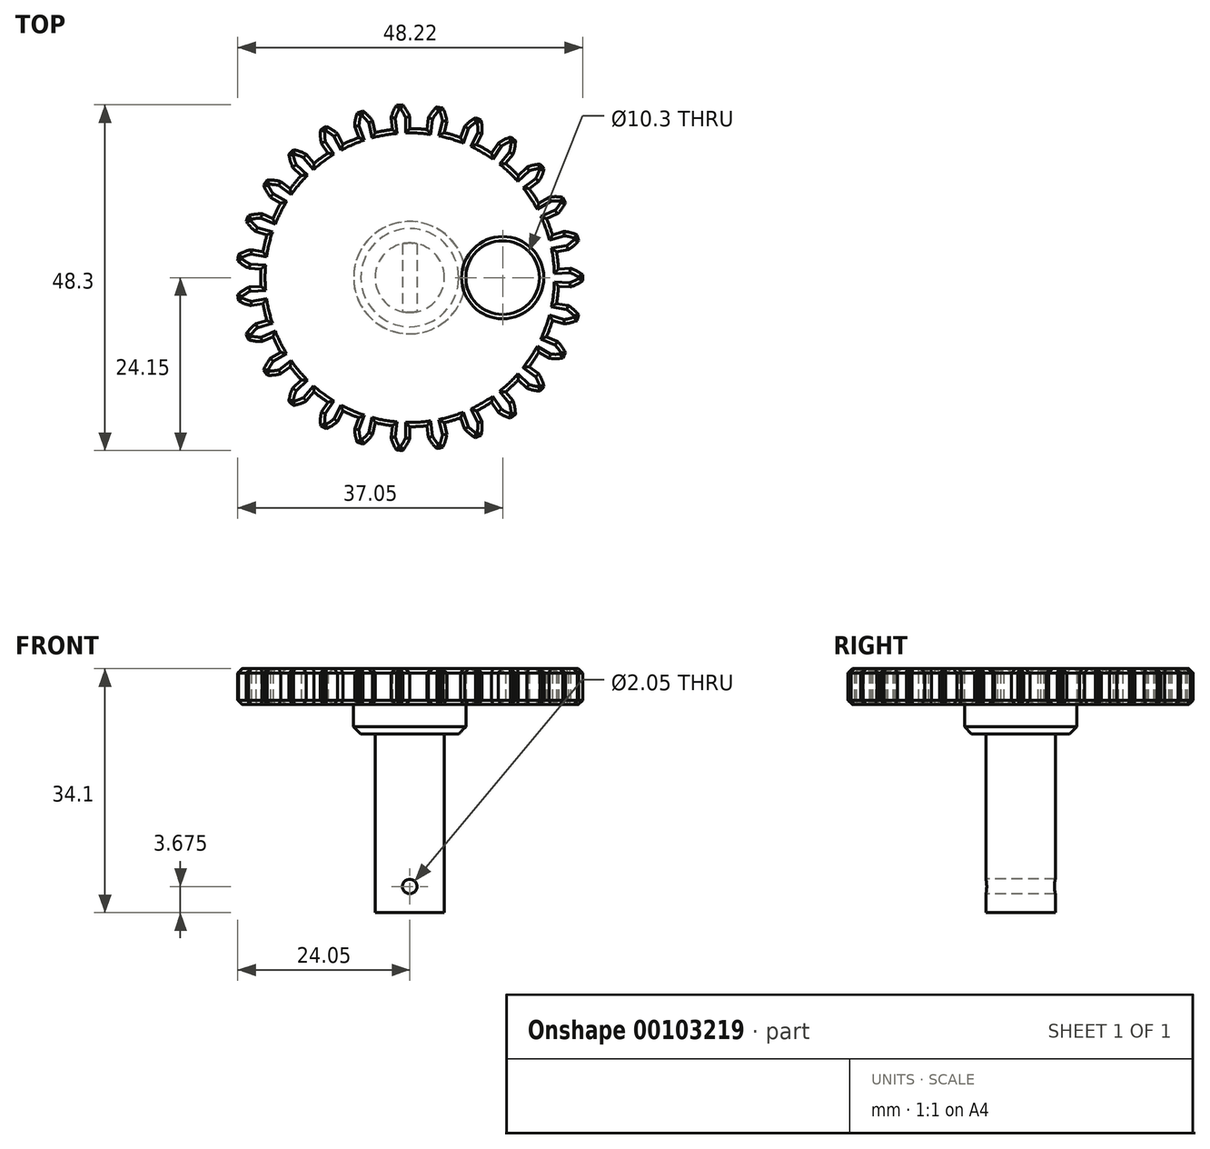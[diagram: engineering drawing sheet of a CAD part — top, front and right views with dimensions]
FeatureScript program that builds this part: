
annotation { "Feature Type Name" : "Feature", "Feature Type Description" : "" }
export const myFeature = defineFeature(function(context is Context, id is Id, definition is map)
    precondition{}
    {
        {
            assignVariable(context, id + "F0", {"name" : "PrintingOffset", "anyValue" : 0.3});
        }
        {
            assignVariable(context, id + "F1", {"name" : "ClampThickness", "anyValue" : 20});
        }
        {
            assignVariable(context, id + "F2", {"name" : "FilamentDiameter", "anyValue" : 1.75 + getVariable(context, 'PrintingOffset')});
        }
        {
            assignVariable(context, id + "F3", {"name" : "CollarThickness", "anyValue" : 2 * getVariable(context, 'FilamentDiameter')});
        }
        {
            assignVariable(context, id + "F4", {"name" : "GearThickness", "anyValue" : 5});
        }
        {
            var Q0;
            Q0=qCreatedBy(makeId("Top.planeOp"),FACE);
            var sketch = newSketch(context, id + "F5", { "sketchPlane" : qUnion([Q0])});
            skCircle(sketch, "E0", {"center": v(0, 0) * mm, "radius": 22.5 * mm, "construction": true});
            skCircle(sketch, "E1", {"center": v(0, 0) * mm, "radius": 20.83 * mm});
            skCircle(sketch, "E2", {"center": v(0, 0) * mm, "radius": 24.17 * mm, "construction": true});
            skLineSegment(sketch, "E3", {"start": v(0, 0) * mm, "end": v(0, 28.6) * mm, "construction": true});
            skLineSegment(sketch, "E4", {"start": v(0, 0) * mm, "end": v(-3.34, 28.6) * mm, "construction": true});
            skLineSegment(sketch, "E5", {"start": v(-15.46, 22.5) * mm, "end": v(0, 22.5) * mm, "construction": true});
            skLineSegment(sketch, "E6", {"start": v(0, 22.5) * mm, "end": v(-15.46, 16.87) * mm, "construction": true});
            skLineSegment(sketch, "E7", {"start": v(0, 0) * mm, "end": v(-1.67, 28.6) * mm, "construction": true});
            skCircle(sketch, "E8", {"center": v(0, 22.5) * mm, "radius": 5.62 * mm, "construction": true});
            skCircle(sketch, "E9", {"center": v(0, 0) * mm, "radius": 21.14 * mm, "construction": true});
            skArc(sketch, "E10", {"start": v(0, 22.5) * mm, "mid": v(-0.42, 23.37) * mm, "end": v(-0.98, 24.15) * mm});
            skArc(sketch, "E11.trimOffspring", {"start": v(0.36, 20.83) * mm, "mid": v(0.35, 20.99) * mm, "end": v(0.34, 21.14) * mm});
            skArc(sketch, "E12.trimOffspring", {"start": v(-0.98, 16.82) * mm, "mid": v(-0.93, 16.88) * mm, "end": v(-0.88, 16.94) * mm});
            skLineSegment(sketch, "E13", {"start": v(0, 22.5) * mm, "end": v(0, 20.83) * mm});
            skLineSegment(sketch, "E14", {"start": v(-0.98, 24.15) * mm, "end": v(-1.4, 24.13) * mm});
            skLineSegment(sketch, "E15.MirrorCS", {"start": v(-1.83, 24.1) * mm, "end": v(-1.4, 24.13) * mm});
            skArc(sketch, "E16.MirrorCS", {"start": v(-2.61, 22.35) * mm, "mid": v(-2.3, 23.26) * mm, "end": v(-1.83, 24.1) * mm});
            skLineSegment(sketch, "E17.MirrorCS", {"start": v(-2.61, 22.35) * mm, "end": v(-2.42, 20.7) * mm});
            skLineSegment(sketch, "E18.1.0", {"start": v(-5.19, 21.9) * mm, "end": v(-4.8, 20.27) * mm});
            skArc(sketch, "E18.1.1", {"start": v(-5.19, 21.9) * mm, "mid": v(-5.8, 22.64) * mm, "end": v(-6.53, 23.27) * mm});
            skLineSegment(sketch, "E18.1.2", {"start": v(-6.53, 23.27) * mm, "end": v(-6.93, 23.15) * mm});
            skLineSegment(sketch, "E18.1.3", {"start": v(-7.33, 23.03) * mm, "end": v(-6.93, 23.15) * mm});
            skArc(sketch, "E18.1.4", {"start": v(-7.7, 21.14) * mm, "mid": v(-7.6, 22.1) * mm, "end": v(-7.33, 23.03) * mm});
            skLineSegment(sketch, "E18.1.5", {"start": v(-7.7, 21.14) * mm, "end": v(-7.13, 19.58) * mm});
            skLineSegment(sketch, "E18.2.0", {"start": v(-10.1, 20.1) * mm, "end": v(-9.35, 18.62) * mm});
            skArc(sketch, "E18.2.1", {"start": v(-10.1, 20.1) * mm, "mid": v(-10.86, 20.7) * mm, "end": v(-11.72, 21.14) * mm});
            skLineSegment(sketch, "E18.2.2", {"start": v(-11.72, 21.14) * mm, "end": v(-12.09, 20.93) * mm});
            skLineSegment(sketch, "E18.2.3", {"start": v(-12.45, 20.71) * mm, "end": v(-12.09, 20.93) * mm});
            skArc(sketch, "E18.2.4", {"start": v(-12.36, 18.8) * mm, "mid": v(-12.49, 19.75) * mm, "end": v(-12.45, 20.71) * mm});
            skLineSegment(sketch, "E18.2.5", {"start": v(-12.36, 18.8) * mm, "end": v(-11.45, 17.4) * mm});
            skLineSegment(sketch, "E18.3.0", {"start": v(-14.46, 17.24) * mm, "end": v(-13.4, 15.96) * mm});
            skArc(sketch, "E18.3.1", {"start": v(-14.46, 17.24) * mm, "mid": v(-15.34, 17.63) * mm, "end": v(-16.27, 17.87) * mm});
            skLineSegment(sketch, "E18.3.2", {"start": v(-16.27, 17.87) * mm, "end": v(-16.59, 17.58) * mm});
            skLineSegment(sketch, "E18.3.3", {"start": v(-16.89, 17.29) * mm, "end": v(-16.59, 17.58) * mm});
            skArc(sketch, "E18.3.4", {"start": v(-16.37, 15.44) * mm, "mid": v(-16.7, 16.34) * mm, "end": v(-16.89, 17.29) * mm});
            skLineSegment(sketch, "E18.3.5", {"start": v(-16.37, 15.44) * mm, "end": v(-15.15, 14.3) * mm});
            skLineSegment(sketch, "E18.4.0", {"start": v(-18.05, 13.44) * mm, "end": v(-16.71, 12.44) * mm});
            skArc(sketch, "E18.4.1", {"start": v(-18.05, 13.44) * mm, "mid": v(-19, 13.62) * mm, "end": v(-19.96, 13.63) * mm});
            skLineSegment(sketch, "E18.4.2", {"start": v(-19.96, 13.63) * mm, "end": v(-20.2, 13.28) * mm});
            skLineSegment(sketch, "E18.4.3", {"start": v(-20.42, 12.93) * mm, "end": v(-20.2, 13.28) * mm});
            skArc(sketch, "E18.4.4", {"start": v(-19.49, 11.25) * mm, "mid": v(-20.02, 12.05) * mm, "end": v(-20.42, 12.93) * mm});
            skLineSegment(sketch, "E18.4.5", {"start": v(-19.49, 11.25) * mm, "end": v(-18.04, 10.42) * mm});
            skLineSegment(sketch, "E18.5.0", {"start": v(-20.66, 8.91) * mm, "end": v(-19.13, 8.25) * mm});
            skArc(sketch, "E18.5.1", {"start": v(-20.66, 8.91) * mm, "mid": v(-21.62, 8.87) * mm, "end": v(-22.56, 8.66) * mm});
            skLineSegment(sketch, "E18.5.2", {"start": v(-22.56, 8.66) * mm, "end": v(-22.71, 8.27) * mm});
            skLineSegment(sketch, "E18.5.3", {"start": v(-22.85, 7.87) * mm, "end": v(-22.71, 8.27) * mm});
            skArc(sketch, "E18.5.4", {"start": v(-21.55, 6.45) * mm, "mid": v(-22.26, 7.1) * mm, "end": v(-22.85, 7.87) * mm});
            skLineSegment(sketch, "E18.5.5", {"start": v(-21.55, 6.45) * mm, "end": v(-19.96, 5.98) * mm});
            skLineSegment(sketch, "E18.6.0", {"start": v(-22.16, 3.9) * mm, "end": v(-20.52, 3.62) * mm});
            skArc(sketch, "E18.6.1", {"start": v(-22.16, 3.9) * mm, "mid": v(-23.08, 3.64) * mm, "end": v(-23.95, 3.22) * mm});
            skLineSegment(sketch, "E18.6.2", {"start": v(-23.95, 3.22) * mm, "end": v(-24, 2.8) * mm});
            skLineSegment(sketch, "E18.6.3", {"start": v(-24.05, 2.39) * mm, "end": v(-24, 2.8) * mm});
            skArc(sketch, "E18.6.4", {"start": v(-22.46, 1.3) * mm, "mid": v(-23.3, 1.78) * mm, "end": v(-24.05, 2.39) * mm});
            skLineSegment(sketch, "E18.6.5", {"start": v(-22.46, 1.3) * mm, "end": v(-20.8, 1.21) * mm});
            skLineSegment(sketch, "E18.7.0", {"start": v(-22.46, -1.3) * mm, "end": v(-20.8, -1.21) * mm});
            skArc(sketch, "E18.7.1", {"start": v(-22.46, -1.3) * mm, "mid": v(-23.3, -1.78) * mm, "end": v(-24.05, -2.39) * mm});
            skLineSegment(sketch, "E18.7.2", {"start": v(-24.05, -2.39) * mm, "end": v(-24, -2.8) * mm});
            skLineSegment(sketch, "E18.7.3", {"start": v(-23.95, -3.22) * mm, "end": v(-24, -2.8) * mm});
            skArc(sketch, "E18.7.4", {"start": v(-22.16, -3.9) * mm, "mid": v(-23.08, -3.64) * mm, "end": v(-23.95, -3.22) * mm});
            skLineSegment(sketch, "E18.7.5", {"start": v(-22.16, -3.9) * mm, "end": v(-20.52, -3.62) * mm});
            skLineSegment(sketch, "E18.8.0", {"start": v(-21.55, -6.45) * mm, "end": v(-19.96, -5.98) * mm});
            skArc(sketch, "E18.8.1", {"start": v(-21.55, -6.45) * mm, "mid": v(-22.26, -7.1) * mm, "end": v(-22.85, -7.87) * mm});
            skLineSegment(sketch, "E18.8.2", {"start": v(-22.85, -7.87) * mm, "end": v(-22.71, -8.27) * mm});
            skLineSegment(sketch, "E18.8.3", {"start": v(-22.56, -8.66) * mm, "end": v(-22.71, -8.27) * mm});
            skArc(sketch, "E18.8.4", {"start": v(-20.66, -8.91) * mm, "mid": v(-21.62, -8.87) * mm, "end": v(-22.56, -8.66) * mm});
            skLineSegment(sketch, "E18.8.5", {"start": v(-20.66, -8.91) * mm, "end": v(-19.13, -8.25) * mm});
            skLineSegment(sketch, "E18.9.0", {"start": v(-19.49, -11.25) * mm, "end": v(-18.04, -10.42) * mm});
            skArc(sketch, "E18.9.1", {"start": v(-19.49, -11.25) * mm, "mid": v(-20.02, -12.05) * mm, "end": v(-20.42, -12.93) * mm});
            skLineSegment(sketch, "E18.9.2", {"start": v(-20.42, -12.93) * mm, "end": v(-20.2, -13.28) * mm});
            skLineSegment(sketch, "E18.9.3", {"start": v(-19.96, -13.63) * mm, "end": v(-20.2, -13.28) * mm});
            skArc(sketch, "E18.9.4", {"start": v(-18.05, -13.44) * mm, "mid": v(-19, -13.62) * mm, "end": v(-19.96, -13.63) * mm});
            skLineSegment(sketch, "E18.9.5", {"start": v(-18.05, -13.44) * mm, "end": v(-16.71, -12.44) * mm});
            skLineSegment(sketch, "E18.10.0", {"start": v(-16.37, -15.44) * mm, "end": v(-15.15, -14.3) * mm});
            skArc(sketch, "E18.10.1", {"start": v(-16.37, -15.44) * mm, "mid": v(-16.7, -16.34) * mm, "end": v(-16.89, -17.29) * mm});
            skLineSegment(sketch, "E18.10.2", {"start": v(-16.89, -17.29) * mm, "end": v(-16.59, -17.58) * mm});
            skLineSegment(sketch, "E18.10.3", {"start": v(-16.27, -17.87) * mm, "end": v(-16.59, -17.58) * mm});
            skArc(sketch, "E18.10.4", {"start": v(-14.46, -17.24) * mm, "mid": v(-15.34, -17.63) * mm, "end": v(-16.27, -17.87) * mm});
            skLineSegment(sketch, "E18.10.5", {"start": v(-14.46, -17.24) * mm, "end": v(-13.4, -15.96) * mm});
            skLineSegment(sketch, "E18.11.0", {"start": v(-12.36, -18.8) * mm, "end": v(-11.45, -17.4) * mm});
            skArc(sketch, "E18.11.1", {"start": v(-12.36, -18.8) * mm, "mid": v(-12.49, -19.75) * mm, "end": v(-12.45, -20.71) * mm});
            skLineSegment(sketch, "E18.11.2", {"start": v(-12.45, -20.71) * mm, "end": v(-12.09, -20.93) * mm});
            skLineSegment(sketch, "E18.11.3", {"start": v(-11.72, -21.14) * mm, "end": v(-12.09, -20.93) * mm});
            skArc(sketch, "E18.11.4", {"start": v(-10.1, -20.1) * mm, "mid": v(-10.86, -20.7) * mm, "end": v(-11.72, -21.14) * mm});
            skLineSegment(sketch, "E18.11.5", {"start": v(-10.1, -20.1) * mm, "end": v(-9.35, -18.62) * mm});
            skLineSegment(sketch, "E18.12.0", {"start": v(-7.7, -21.14) * mm, "end": v(-7.13, -19.58) * mm});
            skArc(sketch, "E18.12.1", {"start": v(-7.7, -21.14) * mm, "mid": v(-7.6, -22.1) * mm, "end": v(-7.33, -23.03) * mm});
            skLineSegment(sketch, "E18.12.2", {"start": v(-7.33, -23.03) * mm, "end": v(-6.93, -23.15) * mm});
            skLineSegment(sketch, "E18.12.3", {"start": v(-6.53, -23.27) * mm, "end": v(-6.93, -23.15) * mm});
            skArc(sketch, "E18.12.4", {"start": v(-5.19, -21.9) * mm, "mid": v(-5.8, -22.64) * mm, "end": v(-6.53, -23.27) * mm});
            skLineSegment(sketch, "E18.12.5", {"start": v(-5.19, -21.9) * mm, "end": v(-4.8, -20.27) * mm});
            skLineSegment(sketch, "E18.13.0", {"start": v(-2.61, -22.35) * mm, "end": v(-2.42, -20.7) * mm});
            skArc(sketch, "E18.13.1", {"start": v(-2.61, -22.35) * mm, "mid": v(-2.3, -23.26) * mm, "end": v(-1.83, -24.1) * mm});
            skLineSegment(sketch, "E18.13.2", {"start": v(-1.83, -24.1) * mm, "end": v(-1.4, -24.13) * mm});
            skLineSegment(sketch, "E18.13.3", {"start": v(-0.98, -24.15) * mm, "end": v(-1.4, -24.13) * mm});
            skArc(sketch, "E18.13.4", {"start": v(0, -22.5) * mm, "mid": v(-0.42, -23.37) * mm, "end": v(-0.98, -24.15) * mm});
            skLineSegment(sketch, "E18.13.5", {"start": v(0, -22.5) * mm, "end": v(0, -20.83) * mm});
            skLineSegment(sketch, "E18.14.0", {"start": v(2.61, -22.35) * mm, "end": v(2.42, -20.7) * mm});
            skArc(sketch, "E18.14.1", {"start": v(2.61, -22.35) * mm, "mid": v(3.13, -23.16) * mm, "end": v(3.78, -23.87) * mm});
            skLineSegment(sketch, "E18.14.2", {"start": v(3.78, -23.87) * mm, "end": v(4.2, -23.8) * mm});
            skLineSegment(sketch, "E18.14.3", {"start": v(4.61, -23.72) * mm, "end": v(4.2, -23.8) * mm});
            skArc(sketch, "E18.14.4", {"start": v(5.19, -21.9) * mm, "mid": v(4.98, -22.83) * mm, "end": v(4.61, -23.72) * mm});
            skLineSegment(sketch, "E18.14.5", {"start": v(5.19, -21.9) * mm, "end": v(4.8, -20.27) * mm});
            skLineSegment(sketch, "E18.15.0", {"start": v(7.7, -21.14) * mm, "end": v(7.13, -19.58) * mm});
            skArc(sketch, "E18.15.1", {"start": v(7.7, -21.14) * mm, "mid": v(8.39, -21.81) * mm, "end": v(9.18, -22.35) * mm});
            skLineSegment(sketch, "E18.15.2", {"start": v(9.18, -22.35) * mm, "end": v(9.57, -22.2) * mm});
            skLineSegment(sketch, "E18.15.3", {"start": v(9.96, -22.02) * mm, "end": v(9.57, -22.2) * mm});
            skArc(sketch, "E18.15.4", {"start": v(10.1, -20.1) * mm, "mid": v(10.11, -21.07) * mm, "end": v(9.96, -22.02) * mm});
            skLineSegment(sketch, "E18.15.5", {"start": v(10.1, -20.1) * mm, "end": v(9.35, -18.62) * mm});
            skLineSegment(sketch, "E18.16.0", {"start": v(12.36, -18.8) * mm, "end": v(11.45, -17.4) * mm});
            skArc(sketch, "E18.16.1", {"start": v(12.36, -18.8) * mm, "mid": v(13.2, -19.3) * mm, "end": v(14.1, -19.63) * mm});
            skLineSegment(sketch, "E18.16.2", {"start": v(14.1, -19.63) * mm, "end": v(14.43, -19.39) * mm});
            skLineSegment(sketch, "E18.16.3", {"start": v(14.77, -19.13) * mm, "end": v(14.43, -19.39) * mm});
            skArc(sketch, "E18.16.4", {"start": v(14.46, -17.24) * mm, "mid": v(14.7, -18.17) * mm, "end": v(14.77, -19.13) * mm});
            skLineSegment(sketch, "E18.16.5", {"start": v(14.46, -17.24) * mm, "end": v(13.4, -15.96) * mm});
            skLineSegment(sketch, "E18.17.0", {"start": v(16.37, -15.44) * mm, "end": v(15.15, -14.3) * mm});
            skArc(sketch, "E18.17.1", {"start": v(16.37, -15.44) * mm, "mid": v(17.28, -15.73) * mm, "end": v(18.24, -15.85) * mm});
            skLineSegment(sketch, "E18.17.2", {"start": v(18.24, -15.85) * mm, "end": v(18.52, -15.54) * mm});
            skLineSegment(sketch, "E18.17.3", {"start": v(18.78, -15.2) * mm, "end": v(18.52, -15.54) * mm});
            skArc(sketch, "E18.17.4", {"start": v(18.05, -13.44) * mm, "mid": v(18.5, -14.3) * mm, "end": v(18.78, -15.2) * mm});
            skLineSegment(sketch, "E18.17.5", {"start": v(18.05, -13.44) * mm, "end": v(16.71, -12.44) * mm});
            skLineSegment(sketch, "E18.18.0", {"start": v(19.49, -11.25) * mm, "end": v(18.04, -10.42) * mm});
            skArc(sketch, "E18.18.1", {"start": v(19.49, -11.25) * mm, "mid": v(20.45, -11.32) * mm, "end": v(21.4, -11.22) * mm});
            skLineSegment(sketch, "E18.18.2", {"start": v(21.4, -11.22) * mm, "end": v(21.6, -10.85) * mm});
            skLineSegment(sketch, "E18.18.3", {"start": v(21.78, -10.47) * mm, "end": v(21.6, -10.85) * mm});
            skArc(sketch, "E18.18.4", {"start": v(20.66, -8.91) * mm, "mid": v(21.29, -9.64) * mm, "end": v(21.78, -10.47) * mm});
            skLineSegment(sketch, "E18.18.5", {"start": v(20.66, -8.91) * mm, "end": v(19.13, -8.25) * mm});
            skLineSegment(sketch, "E18.19.0", {"start": v(21.55, -6.45) * mm, "end": v(19.96, -5.98) * mm});
            skArc(sketch, "E18.19.1", {"start": v(21.55, -6.45) * mm, "mid": v(22.5, -6.3) * mm, "end": v(23.41, -5.98) * mm});
            skLineSegment(sketch, "E18.19.2", {"start": v(23.41, -5.98) * mm, "end": v(23.52, -5.57) * mm});
            skLineSegment(sketch, "E18.19.3", {"start": v(23.6, -5.16) * mm, "end": v(23.52, -5.57) * mm});
            skArc(sketch, "E18.19.4", {"start": v(22.16, -3.9) * mm, "mid": v(22.94, -4.47) * mm, "end": v(23.6, -5.16) * mm});
            skLineSegment(sketch, "E18.19.5", {"start": v(22.16, -3.9) * mm, "end": v(20.52, -3.62) * mm});
            skLineSegment(sketch, "E18.20.0", {"start": v(22.46, -1.3) * mm, "end": v(20.8, -1.21) * mm});
            skArc(sketch, "E18.20.1", {"start": v(22.46, -1.3) * mm, "mid": v(23.35, -0.94) * mm, "end": v(24.16, -0.42) * mm});
            skLineSegment(sketch, "E18.20.2", {"start": v(24.16, -0.42) * mm, "end": v(24.17, 0) * mm});
            skLineSegment(sketch, "E18.20.3", {"start": v(24.16, 0.42) * mm, "end": v(24.17, 0) * mm});
            skArc(sketch, "E18.20.4", {"start": v(22.46, 1.3) * mm, "mid": v(23.35, 0.94) * mm, "end": v(24.16, 0.42) * mm});
            skLineSegment(sketch, "E18.20.5", {"start": v(22.46, 1.3) * mm, "end": v(20.8, 1.21) * mm});
            skLineSegment(sketch, "E18.21.0", {"start": v(22.16, 3.9) * mm, "end": v(20.52, 3.62) * mm});
            skArc(sketch, "E18.21.1", {"start": v(22.16, 3.9) * mm, "mid": v(22.94, 4.47) * mm, "end": v(23.6, 5.16) * mm});
            skLineSegment(sketch, "E18.21.2", {"start": v(23.6, 5.16) * mm, "end": v(23.52, 5.57) * mm});
            skLineSegment(sketch, "E18.21.3", {"start": v(23.41, 5.98) * mm, "end": v(23.52, 5.57) * mm});
            skArc(sketch, "E18.21.4", {"start": v(21.55, 6.45) * mm, "mid": v(22.5, 6.3) * mm, "end": v(23.41, 5.98) * mm});
            skLineSegment(sketch, "E18.21.5", {"start": v(21.55, 6.45) * mm, "end": v(19.96, 5.98) * mm});
            skLineSegment(sketch, "E18.22.0", {"start": v(20.66, 8.91) * mm, "end": v(19.13, 8.25) * mm});
            skArc(sketch, "E18.22.1", {"start": v(20.66, 8.91) * mm, "mid": v(21.29, 9.64) * mm, "end": v(21.78, 10.47) * mm});
            skLineSegment(sketch, "E18.22.2", {"start": v(21.78, 10.47) * mm, "end": v(21.6, 10.85) * mm});
            skLineSegment(sketch, "E18.22.3", {"start": v(21.4, 11.22) * mm, "end": v(21.6, 10.85) * mm});
            skArc(sketch, "E18.22.4", {"start": v(19.49, 11.25) * mm, "mid": v(20.45, 11.32) * mm, "end": v(21.4, 11.22) * mm});
            skLineSegment(sketch, "E18.22.5", {"start": v(19.49, 11.25) * mm, "end": v(18.04, 10.42) * mm});
            skLineSegment(sketch, "E18.23.0", {"start": v(18.05, 13.44) * mm, "end": v(16.71, 12.44) * mm});
            skArc(sketch, "E18.23.1", {"start": v(18.05, 13.44) * mm, "mid": v(18.5, 14.3) * mm, "end": v(18.78, 15.2) * mm});
            skLineSegment(sketch, "E18.23.2", {"start": v(18.78, 15.2) * mm, "end": v(18.52, 15.54) * mm});
            skLineSegment(sketch, "E18.23.3", {"start": v(18.24, 15.85) * mm, "end": v(18.52, 15.54) * mm});
            skArc(sketch, "E18.23.4", {"start": v(16.37, 15.44) * mm, "mid": v(17.28, 15.73) * mm, "end": v(18.24, 15.85) * mm});
            skLineSegment(sketch, "E18.23.5", {"start": v(16.37, 15.44) * mm, "end": v(15.15, 14.3) * mm});
            skLineSegment(sketch, "E18.24.0", {"start": v(14.46, 17.24) * mm, "end": v(13.4, 15.96) * mm});
            skArc(sketch, "E18.24.1", {"start": v(14.46, 17.24) * mm, "mid": v(14.7, 18.17) * mm, "end": v(14.77, 19.13) * mm});
            skLineSegment(sketch, "E18.24.2", {"start": v(14.77, 19.13) * mm, "end": v(14.43, 19.39) * mm});
            skLineSegment(sketch, "E18.24.3", {"start": v(14.1, 19.63) * mm, "end": v(14.43, 19.39) * mm});
            skArc(sketch, "E18.24.4", {"start": v(12.36, 18.8) * mm, "mid": v(13.2, 19.3) * mm, "end": v(14.1, 19.63) * mm});
            skLineSegment(sketch, "E18.24.5", {"start": v(12.36, 18.8) * mm, "end": v(11.45, 17.4) * mm});
            skLineSegment(sketch, "E18.25.0", {"start": v(10.1, 20.1) * mm, "end": v(9.35, 18.62) * mm});
            skArc(sketch, "E18.25.1", {"start": v(10.1, 20.1) * mm, "mid": v(10.11, 21.07) * mm, "end": v(9.96, 22.02) * mm});
            skLineSegment(sketch, "E18.25.2", {"start": v(9.96, 22.02) * mm, "end": v(9.57, 22.2) * mm});
            skLineSegment(sketch, "E18.25.3", {"start": v(9.18, 22.35) * mm, "end": v(9.57, 22.2) * mm});
            skArc(sketch, "E18.25.4", {"start": v(7.7, 21.14) * mm, "mid": v(8.39, 21.81) * mm, "end": v(9.18, 22.35) * mm});
            skLineSegment(sketch, "E18.25.5", {"start": v(7.7, 21.14) * mm, "end": v(7.13, 19.58) * mm});
            skLineSegment(sketch, "E18.26.0", {"start": v(5.19, 21.9) * mm, "end": v(4.8, 20.27) * mm});
            skArc(sketch, "E18.26.1", {"start": v(5.19, 21.9) * mm, "mid": v(4.98, 22.83) * mm, "end": v(4.61, 23.72) * mm});
            skLineSegment(sketch, "E18.26.2", {"start": v(4.61, 23.72) * mm, "end": v(4.2, 23.8) * mm});
            skLineSegment(sketch, "E18.26.3", {"start": v(3.78, 23.87) * mm, "end": v(4.2, 23.8) * mm});
            skArc(sketch, "E18.26.4", {"start": v(2.61, 22.35) * mm, "mid": v(3.13, 23.16) * mm, "end": v(3.78, 23.87) * mm});
            skLineSegment(sketch, "E18.26.5", {"start": v(2.61, 22.35) * mm, "end": v(2.42, 20.7) * mm});
            skCircle(sketch, "E19", {"center": v(0, 0) * mm, "radius": 4.85 * mm});
            skCircle(sketch, "E20.0", {"center": v(0, 0) * mm, "radius": 7.85 * mm});
            skCircle(sketch, "E21", {"center": v(13, 0) * mm, "radius": 5.15 * mm});
            skSolve(sketch);
        }
        {
            var Q0;
            {var subQ0=sQuery(id+"F5.wireOp",EDGE,"E18.2.0");Q0=makeQuery(id+"F5.imprint","IMPRINT",FACE,{"disambiguationData":[TD([[makeQuery(id+"F5.imprint","IMPRINT",EDGE,{"derivedFrom":subQ0}),-1.0]])]});}
            var Q1;
            {var subQ0=sQuery(id+"F5.wireOp",EDGE,"E18.23.0");Q1=makeQuery(id+"F5.imprint","IMPRINT",FACE,{"disambiguationData":[TD([[makeQuery(id+"F5.imprint","IMPRINT",EDGE,{"derivedFrom":subQ0}),-1.0]])]});}
            var Q2;
            {var subQ0=sQuery(id+"F5.wireOp",EDGE,"E18.24.0");Q2=makeQuery(id+"F5.imprint","IMPRINT",FACE,{"disambiguationData":[TD([[makeQuery(id+"F5.imprint","IMPRINT",EDGE,{"derivedFrom":subQ0}),-1.0]])]});}
            var Q3;
            {var subQ0=sQuery(id+"F5.wireOp",EDGE,"E18.25.0");Q3=makeQuery(id+"F5.imprint","IMPRINT",FACE,{"disambiguationData":[TD([[makeQuery(id+"F5.imprint","IMPRINT",EDGE,{"derivedFrom":subQ0}),-1.0]])]});}
            var Q4;
            {var subQ0=sQuery(id+"F5.wireOp",EDGE,"E18.26.0");Q4=makeQuery(id+"F5.imprint","IMPRINT",FACE,{"disambiguationData":[TD([[makeQuery(id+"F5.imprint","IMPRINT",EDGE,{"derivedFrom":subQ0}),-1.0]])]});}
            var Q5;
            {var subQ0=sQuery(id+"F5.wireOp",EDGE,"E18.27.0");Q5=makeQuery(id+"F5.imprint","IMPRINT",FACE,{"disambiguationData":[TD([[makeQuery(id+"F5.imprint","IMPRINT",EDGE,{"derivedFrom":subQ0}),-1.0]])]});}
            var Q6;
            {var subQ0=sQuery(id+"F5.wireOp",EDGE,"E18.28.0");Q6=makeQuery(id+"F5.imprint","IMPRINT",FACE,{"disambiguationData":[TD([[makeQuery(id+"F5.imprint","IMPRINT",EDGE,{"derivedFrom":subQ0}),-1.0]])]});}
            var Q7;
            {var subQ0=sQuery(id+"F5.wireOp",EDGE,"E18.29.0");Q7=makeQuery(id+"F5.imprint","IMPRINT",FACE,{"disambiguationData":[TD([[makeQuery(id+"F5.imprint","IMPRINT",EDGE,{"derivedFrom":subQ0}),-1.0]])]});}
            var Q8;
            Q8=makeQuery(id+"F5.imprint","IMPRINT",FACE,{"disambiguationData":[TD([[makeQuery(id+"F5.imprint","IMPRINT",EDGE,{"derivedFrom":sQuery(id+"F5.wireOp",EDGE,"E10")}),1.0]])]});
            var Q9;
            {var subQ0=sQuery(id+"F5.wireOp",EDGE,"E18.1.0");Q9=makeQuery(id+"F5.imprint","IMPRINT",FACE,{"disambiguationData":[TD([[makeQuery(id+"F5.imprint","IMPRINT",EDGE,{"derivedFrom":subQ0}),-1.0]])]});}
            var Q10;
            {var subQ0=sQuery(id+"F5.wireOp",EDGE,"E18.3.0");Q10=makeQuery(id+"F5.imprint","IMPRINT",FACE,{"disambiguationData":[TD([[makeQuery(id+"F5.imprint","IMPRINT",EDGE,{"derivedFrom":subQ0}),-1.0]])]});}
            var Q11;
            {var subQ0=sQuery(id+"F5.wireOp",EDGE,"E18.4.0");Q11=makeQuery(id+"F5.imprint","IMPRINT",FACE,{"disambiguationData":[TD([[makeQuery(id+"F5.imprint","IMPRINT",EDGE,{"derivedFrom":subQ0}),-1.0]])]});}
            var Q12;
            {var subQ0=sQuery(id+"F5.wireOp",EDGE,"E18.5.0");Q12=makeQuery(id+"F5.imprint","IMPRINT",FACE,{"disambiguationData":[TD([[makeQuery(id+"F5.imprint","IMPRINT",EDGE,{"derivedFrom":subQ0}),-1.0]])]});}
            var Q13;
            {var subQ0=sQuery(id+"F5.wireOp",EDGE,"E18.6.0");Q13=makeQuery(id+"F5.imprint","IMPRINT",FACE,{"disambiguationData":[TD([[makeQuery(id+"F5.imprint","IMPRINT",EDGE,{"derivedFrom":subQ0}),-1.0]])]});}
            var Q14;
            {var subQ0=sQuery(id+"F5.wireOp",EDGE,"E18.7.0");Q14=makeQuery(id+"F5.imprint","IMPRINT",FACE,{"disambiguationData":[TD([[makeQuery(id+"F5.imprint","IMPRINT",EDGE,{"derivedFrom":subQ0}),-1.0]])]});}
            var Q15;
            {var subQ0=sQuery(id+"F5.wireOp",EDGE,"E18.8.0");Q15=makeQuery(id+"F5.imprint","IMPRINT",FACE,{"disambiguationData":[TD([[makeQuery(id+"F5.imprint","IMPRINT",EDGE,{"derivedFrom":subQ0}),-1.0]])]});}
            var Q16;
            {var subQ0=sQuery(id+"F5.wireOp",EDGE,"E18.9.0");Q16=makeQuery(id+"F5.imprint","IMPRINT",FACE,{"disambiguationData":[TD([[makeQuery(id+"F5.imprint","IMPRINT",EDGE,{"derivedFrom":subQ0}),-1.0]])]});}
            var Q17;
            {var subQ0=sQuery(id+"F5.wireOp",EDGE,"E18.10.0");Q17=makeQuery(id+"F5.imprint","IMPRINT",FACE,{"disambiguationData":[TD([[makeQuery(id+"F5.imprint","IMPRINT",EDGE,{"derivedFrom":subQ0}),-1.0]])]});}
            var Q18;
            {var subQ0=sQuery(id+"F5.wireOp",EDGE,"E18.11.0");Q18=makeQuery(id+"F5.imprint","IMPRINT",FACE,{"disambiguationData":[TD([[makeQuery(id+"F5.imprint","IMPRINT",EDGE,{"derivedFrom":subQ0}),-1.0]])]});}
            var Q19;
            {var subQ1=sQuery(id+"F5.wireOp",EDGE,"E18.12.0");Q19=makeQuery(id+"F5.imprint","IMPRINT",FACE,{"disambiguationData":[TD([[makeQuery(id+"F5.imprint","IMPRINT",EDGE,{"derivedFrom":subQ1}),-1.0]])]});}
            var Q20;
            {var subQ0=sQuery(id+"F5.wireOp",EDGE,"E18.13.0");Q20=makeQuery(id+"F5.imprint","IMPRINT",FACE,{"disambiguationData":[TD([[makeQuery(id+"F5.imprint","IMPRINT",EDGE,{"derivedFrom":subQ0}),-1.0]])]});}
            var Q21;
            {var subQ0=sQuery(id+"F5.wireOp",EDGE,"E18.14.0");Q21=makeQuery(id+"F5.imprint","IMPRINT",FACE,{"disambiguationData":[TD([[makeQuery(id+"F5.imprint","IMPRINT",EDGE,{"derivedFrom":subQ0}),-1.0]])]});}
            var Q22;
            {var subQ0=sQuery(id+"F5.wireOp",EDGE,"E18.15.0");Q22=makeQuery(id+"F5.imprint","IMPRINT",FACE,{"disambiguationData":[TD([[makeQuery(id+"F5.imprint","IMPRINT",EDGE,{"derivedFrom":subQ0}),-1.0]])]});}
            var Q23;
            {var subQ0=sQuery(id+"F5.wireOp",EDGE,"E18.16.0");Q23=makeQuery(id+"F5.imprint","IMPRINT",FACE,{"disambiguationData":[TD([[makeQuery(id+"F5.imprint","IMPRINT",EDGE,{"derivedFrom":subQ0}),-1.0]])]});}
            var Q24;
            {var subQ0=sQuery(id+"F5.wireOp",EDGE,"E18.17.0");Q24=makeQuery(id+"F5.imprint","IMPRINT",FACE,{"disambiguationData":[TD([[makeQuery(id+"F5.imprint","IMPRINT",EDGE,{"derivedFrom":subQ0}),-1.0]])]});}
            var Q25;
            {var subQ0=sQuery(id+"F5.wireOp",EDGE,"E18.18.0");Q25=makeQuery(id+"F5.imprint","IMPRINT",FACE,{"disambiguationData":[TD([[makeQuery(id+"F5.imprint","IMPRINT",EDGE,{"derivedFrom":subQ0}),-1.0]])]});}
            var Q26;
            {var subQ0=sQuery(id+"F5.wireOp",EDGE,"E18.19.0");Q26=makeQuery(id+"F5.imprint","IMPRINT",FACE,{"disambiguationData":[TD([[makeQuery(id+"F5.imprint","IMPRINT",EDGE,{"derivedFrom":subQ0}),-1.0]])]});}
            var Q27;
            {var subQ0=sQuery(id+"F5.wireOp",EDGE,"E18.20.0");Q27=makeQuery(id+"F5.imprint","IMPRINT",FACE,{"disambiguationData":[TD([[makeQuery(id+"F5.imprint","IMPRINT",EDGE,{"derivedFrom":subQ0}),-1.0]])]});}
            var Q28;
            {var subQ0=sQuery(id+"F5.wireOp",EDGE,"E18.21.0");Q28=makeQuery(id+"F5.imprint","IMPRINT",FACE,{"disambiguationData":[TD([[makeQuery(id+"F5.imprint","IMPRINT",EDGE,{"derivedFrom":subQ0}),-1.0]])]});}
            var Q29;
            {var subQ0=sQuery(id+"F5.wireOp",EDGE,"E18.22.0");Q29=makeQuery(id+"F5.imprint","IMPRINT",FACE,{"disambiguationData":[TD([[makeQuery(id+"F5.imprint","IMPRINT",EDGE,{"derivedFrom":subQ0}),-1.0]])]});}
            var Q30;
            Q30=makeQuery(id+"F5.imprint","IMPRINT",FACE,{"disambiguationData":[TD([[makeQuery(id+"F5.imprint","IMPRINT",EDGE,{"derivedFrom":sQuery(id+"F5.wireOp",EDGE,"E20.0")}),-1.0]])]});
            var Q31;
            Q31=makeQuery(id+"F5.imprint","IMPRINT",FACE,{"disambiguationData":[TD([[makeQuery(id+"F5.imprint","IMPRINT",EDGE,{"derivedFrom":sQuery(id+"F5.wireOp",EDGE,"E19")}),-1.0]])]});
            var Q32;
            Q32=makeQuery(id+"F5.imprint","IMPRINT",FACE,{"disambiguationData":[TD([[makeQuery(id+"F5.imprint","IMPRINT",EDGE,{"derivedFrom":sQuery(id+"F5.wireOp",EDGE,"E19")}),1.0]])]});
            extrude(context, id + "F6", {"entities" : qUnion([Q0, Q1, Q2, Q3, Q4, Q5, Q6, Q7, Q8, Q9, Q10, Q11, Q12, Q13, Q14, Q15, Q16, Q17, Q18, Q19, Q20, Q21, Q22, Q23, Q24, Q25, Q26, Q27, Q28, Q29, Q30, Q31, Q32]), "depth" : (getVariable(context, 'GearThickness')) * mm});
        }
        {
            var Q0;
            Q0=makeQuery(id+"F6.opExtrude","CAP_FACE",FACE,{"disambiguationData":[OSD([sQuery(id+"F5.wireOp",EDGE,"E1"),sQuery(id+"F5.wireOp",EDGE,"E10"),sQuery(id+"F5.wireOp",EDGE,"E13"),sQuery(id+"F5.wireOp",EDGE,"E14"),sQuery(id+"F5.wireOp",EDGE,"E15.MirrorCS"),sQuery(id+"F5.wireOp",EDGE,"E16.MirrorCS"),sQuery(id+"F5.wireOp",EDGE,"E17.MirrorCS"),sQuery(id+"F5.wireOp",EDGE,"E18.1.0"),sQuery(id+"F5.wireOp",EDGE,"E18.1.1"),sQuery(id+"F5.wireOp",EDGE,"E18.1.2"),sQuery(id+"F5.wireOp",EDGE,"E18.1.3"),sQuery(id+"F5.wireOp",EDGE,"E18.1.4"),sQuery(id+"F5.wireOp",EDGE,"E18.1.5"),sQuery(id+"F5.wireOp",EDGE,"E18.2.0"),sQuery(id+"F5.wireOp",EDGE,"E18.2.1"),sQuery(id+"F5.wireOp",EDGE,"E18.2.2"),sQuery(id+"F5.wireOp",EDGE,"E18.2.3"),sQuery(id+"F5.wireOp",EDGE,"E18.2.4"),sQuery(id+"F5.wireOp",EDGE,"E18.2.5"),sQuery(id+"F5.wireOp",EDGE,"E18.3.0"),sQuery(id+"F5.wireOp",EDGE,"E18.3.1"),sQuery(id+"F5.wireOp",EDGE,"E18.3.2"),sQuery(id+"F5.wireOp",EDGE,"E18.3.3"),sQuery(id+"F5.wireOp",EDGE,"E18.3.4"),sQuery(id+"F5.wireOp",EDGE,"E18.3.5"),sQuery(id+"F5.wireOp",EDGE,"E18.4.0"),sQuery(id+"F5.wireOp",EDGE,"E18.4.1"),sQuery(id+"F5.wireOp",EDGE,"E18.4.2"),sQuery(id+"F5.wireOp",EDGE,"E18.4.3"),sQuery(id+"F5.wireOp",EDGE,"E18.4.4"),sQuery(id+"F5.wireOp",EDGE,"E18.4.5"),sQuery(id+"F5.wireOp",EDGE,"E18.5.0"),sQuery(id+"F5.wireOp",EDGE,"E18.5.1"),sQuery(id+"F5.wireOp",EDGE,"E18.5.2"),sQuery(id+"F5.wireOp",EDGE,"E18.5.3"),sQuery(id+"F5.wireOp",EDGE,"E18.5.4"),sQuery(id+"F5.wireOp",EDGE,"E18.5.5"),sQuery(id+"F5.wireOp",EDGE,"E18.6.0"),sQuery(id+"F5.wireOp",EDGE,"E18.6.1"),sQuery(id+"F5.wireOp",EDGE,"E18.6.2"),sQuery(id+"F5.wireOp",EDGE,"E18.6.3"),sQuery(id+"F5.wireOp",EDGE,"E18.6.4"),sQuery(id+"F5.wireOp",EDGE,"E18.6.5"),sQuery(id+"F5.wireOp",EDGE,"E18.7.0"),sQuery(id+"F5.wireOp",EDGE,"E18.7.1"),sQuery(id+"F5.wireOp",EDGE,"E18.7.2"),sQuery(id+"F5.wireOp",EDGE,"E18.7.3"),sQuery(id+"F5.wireOp",EDGE,"E18.7.4"),sQuery(id+"F5.wireOp",EDGE,"E18.7.5"),sQuery(id+"F5.wireOp",EDGE,"E18.8.0"),sQuery(id+"F5.wireOp",EDGE,"E18.8.1"),sQuery(id+"F5.wireOp",EDGE,"E18.8.2"),sQuery(id+"F5.wireOp",EDGE,"E18.8.3"),sQuery(id+"F5.wireOp",EDGE,"E18.8.4"),sQuery(id+"F5.wireOp",EDGE,"E18.8.5"),sQuery(id+"F5.wireOp",EDGE,"E18.9.0"),sQuery(id+"F5.wireOp",EDGE,"E18.9.1"),sQuery(id+"F5.wireOp",EDGE,"E18.9.2"),sQuery(id+"F5.wireOp",EDGE,"E18.9.3"),sQuery(id+"F5.wireOp",EDGE,"E18.9.4"),sQuery(id+"F5.wireOp",EDGE,"E18.9.5"),sQuery(id+"F5.wireOp",EDGE,"E18.10.0"),sQuery(id+"F5.wireOp",EDGE,"E18.10.1"),sQuery(id+"F5.wireOp",EDGE,"E18.10.2"),sQuery(id+"F5.wireOp",EDGE,"E18.10.3"),sQuery(id+"F5.wireOp",EDGE,"E18.10.4"),sQuery(id+"F5.wireOp",EDGE,"E18.10.5"),sQuery(id+"F5.wireOp",EDGE,"E18.11.0"),sQuery(id+"F5.wireOp",EDGE,"E18.11.1"),sQuery(id+"F5.wireOp",EDGE,"E18.11.2"),sQuery(id+"F5.wireOp",EDGE,"E18.11.3"),sQuery(id+"F5.wireOp",EDGE,"E18.11.4"),sQuery(id+"F5.wireOp",EDGE,"E18.11.5"),sQuery(id+"F5.wireOp",EDGE,"E18.12.0"),sQuery(id+"F5.wireOp",EDGE,"E18.12.1"),sQuery(id+"F5.wireOp",EDGE,"E18.12.2"),sQuery(id+"F5.wireOp",EDGE,"E18.12.3"),sQuery(id+"F5.wireOp",EDGE,"E18.12.4"),sQuery(id+"F5.wireOp",EDGE,"E18.12.5"),sQuery(id+"F5.wireOp",EDGE,"E18.13.0"),sQuery(id+"F5.wireOp",EDGE,"E18.13.1"),sQuery(id+"F5.wireOp",EDGE,"E18.13.2"),sQuery(id+"F5.wireOp",EDGE,"E18.13.3"),sQuery(id+"F5.wireOp",EDGE,"E18.13.4"),sQuery(id+"F5.wireOp",EDGE,"E18.13.5"),sQuery(id+"F5.wireOp",EDGE,"E18.14.0"),sQuery(id+"F5.wireOp",EDGE,"E18.14.1"),sQuery(id+"F5.wireOp",EDGE,"E18.14.2"),sQuery(id+"F5.wireOp",EDGE,"E18.14.3"),sQuery(id+"F5.wireOp",EDGE,"E18.14.4"),sQuery(id+"F5.wireOp",EDGE,"E18.14.5"),sQuery(id+"F5.wireOp",EDGE,"E18.15.0"),sQuery(id+"F5.wireOp",EDGE,"E18.15.1"),sQuery(id+"F5.wireOp",EDGE,"E18.15.2"),sQuery(id+"F5.wireOp",EDGE,"E18.15.3"),sQuery(id+"F5.wireOp",EDGE,"E18.15.4"),sQuery(id+"F5.wireOp",EDGE,"E18.15.5"),sQuery(id+"F5.wireOp",EDGE,"E18.16.0"),sQuery(id+"F5.wireOp",EDGE,"E18.16.1"),sQuery(id+"F5.wireOp",EDGE,"E18.16.2"),sQuery(id+"F5.wireOp",EDGE,"E18.16.3"),sQuery(id+"F5.wireOp",EDGE,"E18.16.4"),sQuery(id+"F5.wireOp",EDGE,"E18.16.5"),sQuery(id+"F5.wireOp",EDGE,"E18.17.0"),sQuery(id+"F5.wireOp",EDGE,"E18.17.1"),sQuery(id+"F5.wireOp",EDGE,"E18.17.2"),sQuery(id+"F5.wireOp",EDGE,"E18.17.3"),sQuery(id+"F5.wireOp",EDGE,"E18.17.4"),sQuery(id+"F5.wireOp",EDGE,"E18.17.5"),sQuery(id+"F5.wireOp",EDGE,"E18.18.0"),sQuery(id+"F5.wireOp",EDGE,"E18.18.1"),sQuery(id+"F5.wireOp",EDGE,"E18.18.2"),sQuery(id+"F5.wireOp",EDGE,"E18.18.3"),sQuery(id+"F5.wireOp",EDGE,"E18.18.4"),sQuery(id+"F5.wireOp",EDGE,"E18.18.5"),sQuery(id+"F5.wireOp",EDGE,"E18.19.0"),sQuery(id+"F5.wireOp",EDGE,"E18.19.1"),sQuery(id+"F5.wireOp",EDGE,"E18.19.2"),sQuery(id+"F5.wireOp",EDGE,"E18.19.3"),sQuery(id+"F5.wireOp",EDGE,"E18.19.4"),sQuery(id+"F5.wireOp",EDGE,"E18.19.5"),sQuery(id+"F5.wireOp",EDGE,"E18.20.0"),sQuery(id+"F5.wireOp",EDGE,"E18.20.1"),sQuery(id+"F5.wireOp",EDGE,"E18.20.2"),sQuery(id+"F5.wireOp",EDGE,"E18.20.3"),sQuery(id+"F5.wireOp",EDGE,"E18.20.4"),sQuery(id+"F5.wireOp",EDGE,"E18.20.5"),sQuery(id+"F5.wireOp",EDGE,"E18.21.0"),sQuery(id+"F5.wireOp",EDGE,"E18.21.1"),sQuery(id+"F5.wireOp",EDGE,"E18.21.2"),sQuery(id+"F5.wireOp",EDGE,"E18.21.3"),sQuery(id+"F5.wireOp",EDGE,"E18.21.4"),sQuery(id+"F5.wireOp",EDGE,"E18.21.5"),sQuery(id+"F5.wireOp",EDGE,"E18.22.0"),sQuery(id+"F5.wireOp",EDGE,"E18.22.1"),sQuery(id+"F5.wireOp",EDGE,"E18.22.2"),sQuery(id+"F5.wireOp",EDGE,"E18.22.3"),sQuery(id+"F5.wireOp",EDGE,"E18.22.4"),sQuery(id+"F5.wireOp",EDGE,"E18.22.5"),sQuery(id+"F5.wireOp",EDGE,"E18.23.0"),sQuery(id+"F5.wireOp",EDGE,"E18.23.1"),sQuery(id+"F5.wireOp",EDGE,"E18.23.2"),sQuery(id+"F5.wireOp",EDGE,"E18.23.3"),sQuery(id+"F5.wireOp",EDGE,"E18.23.4"),sQuery(id+"F5.wireOp",EDGE,"E18.23.5"),sQuery(id+"F5.wireOp",EDGE,"E18.24.0"),sQuery(id+"F5.wireOp",EDGE,"E18.24.1"),sQuery(id+"F5.wireOp",EDGE,"E18.24.2"),sQuery(id+"F5.wireOp",EDGE,"E18.24.3"),sQuery(id+"F5.wireOp",EDGE,"E18.24.4"),sQuery(id+"F5.wireOp",EDGE,"E18.24.5"),sQuery(id+"F5.wireOp",EDGE,"E18.25.0"),sQuery(id+"F5.wireOp",EDGE,"E18.25.1"),sQuery(id+"F5.wireOp",EDGE,"E18.25.2"),sQuery(id+"F5.wireOp",EDGE,"E18.25.3"),sQuery(id+"F5.wireOp",EDGE,"E18.25.4"),sQuery(id+"F5.wireOp",EDGE,"E18.25.5"),sQuery(id+"F5.wireOp",EDGE,"E18.26.0"),sQuery(id+"F5.wireOp",EDGE,"E18.26.1"),sQuery(id+"F5.wireOp",EDGE,"E18.26.2"),sQuery(id+"F5.wireOp",EDGE,"E18.26.3"),sQuery(id+"F5.wireOp",EDGE,"E18.26.4"),sQuery(id+"F5.wireOp",EDGE,"E18.26.5"),sQuery(id+"F5.wireOp",EDGE,"E21")])],"isStart":false});
            var Q1;
            {var subQ0=sQuery(id+"F5.wireOp",EDGE,"E18.10.1");var subQ1=sQuery(id+"F5.wireOp",EDGE,"E18.21.0");var subQ2=sQuery(id+"F5.wireOp",EDGE,"E18.9.5");var subQ3=sQuery(id+"F5.wireOp",EDGE,"E18.25.3");var subQ4=sQuery(id+"F5.wireOp",EDGE,"E18.9.3");var subQ5=sQuery(id+"F5.wireOp",EDGE,"E18.4.4");var subQ6=sQuery(id+"F5.wireOp",EDGE,"E18.20.2");var subQ7=sQuery(id+"F5.wireOp",EDGE,"E18.9.2");var subQ8=sQuery(id+"F5.wireOp",EDGE,"E18.9.1");var subQ9=sQuery(id+"F5.wireOp",EDGE,"E18.7.4");var subQ10=sQuery(id+"F5.wireOp",EDGE,"E18.7.3");var subQ11=sQuery(id+"F5.wireOp",EDGE,"E18.15.5");var subQ12=sQuery(id+"F5.wireOp",EDGE,"E18.7.2");var subQ13=sQuery(id+"F5.wireOp",EDGE,"E18.23.0");var subQ14=sQuery(id+"F5.wireOp",EDGE,"E18.7.0");var subQ15=sQuery(id+"F5.wireOp",EDGE,"E18.10.3");var subQ16=sQuery(id+"F5.wireOp",EDGE,"E18.2.1");var subQ17=sQuery(id+"F5.wireOp",EDGE,"E18.6.5");var subQ18=sQuery(id+"F5.wireOp",EDGE,"E18.6.4");var subQ19=sQuery(id+"F5.wireOp",EDGE,"E18.5.3");var subQ20=sQuery(id+"F5.wireOp",EDGE,"E18.5.0");var subQ21=sQuery(id+"F5.wireOp",EDGE,"E18.8.3");var subQ22=sQuery(id+"F5.wireOp",EDGE,"E18.13.2");var subQ23=sQuery(id+"F5.wireOp",EDGE,"E18.4.5");var subQ24=sQuery(id+"F5.wireOp",EDGE,"E18.4.3");var subQ25=sQuery(id+"F5.wireOp",EDGE,"E18.15.2");var subQ26=sQuery(id+"F5.wireOp",EDGE,"E18.8.0");var subQ27=sQuery(id+"F5.wireOp",EDGE,"E18.18.5");var subQ28=sQuery(id+"F5.wireOp",EDGE,"E1");var subQ29=sQuery(id+"F5.wireOp",EDGE,"E18.19.0");var subQ30=sQuery(id+"F5.wireOp",EDGE,"E18.4.2");var subQ31=sQuery(id+"F5.wireOp",EDGE,"E18.7.5");var subQ32=sQuery(id+"F5.wireOp",EDGE,"E18.4.1");var subQ33=sQuery(id+"F5.wireOp",EDGE,"E18.4.0");var subQ34=sQuery(id+"F5.wireOp",EDGE,"E18.8.5");var subQ35=sQuery(id+"F5.wireOp",EDGE,"E18.3.5");var subQ36=sQuery(id+"F5.wireOp",EDGE,"E18.3.4");var subQ37=sQuery(id+"F5.wireOp",EDGE,"E18.3.3");var subQ38=sQuery(id+"F5.wireOp",EDGE,"E18.8.2");var subQ39=sQuery(id+"F5.wireOp",EDGE,"E18.3.2");var subQ40=sQuery(id+"F5.wireOp",EDGE,"E18.8.1");var subQ41=sQuery(id+"F5.wireOp",EDGE,"E18.13.5");var subQ42=sQuery(id+"F5.wireOp",EDGE,"E18.14.0");var subQ43=sQuery(id+"F5.wireOp",EDGE,"E18.6.1");var subQ44=sQuery(id+"F5.wireOp",EDGE,"E18.5.5");var subQ45=sQuery(id+"F5.wireOp",EDGE,"E18.6.0");var subQ46=sQuery(id+"F5.wireOp",EDGE,"E18.6.2");var subQ47=sQuery(id+"F5.wireOp",EDGE,"E18.1.3");var subQ48=sQuery(id+"F5.wireOp",EDGE,"E18.12.5");var subQ49=sQuery(id+"F5.wireOp",EDGE,"E18.13.0");var subQ50=sQuery(id+"F5.wireOp",EDGE,"E18.14.5");var subQ51=sQuery(id+"F5.wireOp",EDGE,"E18.15.0");var subQ52=sQuery(id+"F5.wireOp",EDGE,"E14");var subQ53=sQuery(id+"F5.wireOp",EDGE,"E18.11.5");var subQ54=sQuery(id+"F5.wireOp",EDGE,"E18.12.0");var subQ55=sQuery(id+"F5.wireOp",EDGE,"E18.10.5");var subQ56=sQuery(id+"F5.wireOp",EDGE,"E18.10.4");var subQ57=sQuery(id+"F5.wireOp",EDGE,"E18.2.0");var subQ58=sQuery(id+"F5.wireOp",EDGE,"E18.11.0");var subQ59=sQuery(id+"F5.wireOp",EDGE,"E18.5.1");var subQ60=sQuery(id+"F5.wireOp",EDGE,"E18.16.0");var subQ61=sQuery(id+"F5.wireOp",EDGE,"E18.20.5");var subQ62=sQuery(id+"F5.wireOp",EDGE,"E18.9.0");var subQ63=sQuery(id+"F5.wireOp",EDGE,"E18.23.5");var subQ64=sQuery(id+"F5.wireOp",EDGE,"E18.24.0");var subQ65=sQuery(id+"F5.wireOp",EDGE,"E18.11.1");var subQ66=sQuery(id+"F5.wireOp",EDGE,"E18.13.4");var subQ67=sQuery(id+"F5.wireOp",EDGE,"E18.2.3");var subQ68=sQuery(id+"F5.wireOp",EDGE,"E18.18.1");var subQ69=sQuery(id+"F5.wireOp",EDGE,"E18.22.5");var subQ70=sQuery(id+"F5.wireOp",EDGE,"E16.MirrorCS");var subQ71=sQuery(id+"F5.wireOp",EDGE,"E18.6.3");var subQ72=sQuery(id+"F5.wireOp",EDGE,"E18.11.2");var subQ73=sQuery(id+"F5.wireOp",EDGE,"E18.21.5");var subQ74=sQuery(id+"F5.wireOp",EDGE,"E18.22.0");var subQ75=sQuery(id+"F5.wireOp",EDGE,"E18.1.5");var subQ76=sQuery(id+"F5.wireOp",EDGE,"E18.10.0");var subQ77=sQuery(id+"F5.wireOp",EDGE,"E18.24.5");var subQ78=sQuery(id+"F5.wireOp",EDGE,"E18.25.0");var subQ79=sQuery(id+"F5.wireOp",EDGE,"E18.7.1");var subQ80=sQuery(id+"F5.wireOp",EDGE,"E18.25.5");var subQ81=sQuery(id+"F5.wireOp",EDGE,"E18.26.0");var subQ83=sQuery(id+"F5.wireOp",EDGE,"E13");var subQ84=sQuery(id+"F5.wireOp",EDGE,"E18.26.5");var subQ85=sQuery(id+"F5.wireOp",EDGE,"E18.1.2");var subQ86=sQuery(id+"F5.wireOp",EDGE,"E18.25.4");var subQ87=sQuery(id+"F5.wireOp",EDGE,"E18.5.2");var subQ88=sQuery(id+"F5.wireOp",EDGE,"E17.MirrorCS");var subQ89=sQuery(id+"F5.wireOp",EDGE,"E18.1.0");var subQ90=sQuery(id+"F5.wireOp",EDGE,"E18.5.4");var subQ91=sQuery(id+"F5.wireOp",EDGE,"E18.2.5");var subQ92=sQuery(id+"F5.wireOp",EDGE,"E18.3.0");var subQ93=sQuery(id+"F5.wireOp",EDGE,"E18.16.5");var subQ94=sQuery(id+"F5.wireOp",EDGE,"E18.17.0");var subQ95=sQuery(id+"F5.wireOp",EDGE,"E18.17.5");var subQ96=sQuery(id+"F5.wireOp",EDGE,"E18.18.0");var subQ97=sQuery(id+"F5.wireOp",EDGE,"E18.10.2");var subQ98=sQuery(id+"F5.wireOp",EDGE,"E18.19.5");var subQ99=sQuery(id+"F5.wireOp",EDGE,"E18.20.0");var subQ100=sQuery(id+"F5.wireOp",EDGE,"E18.15.3");var subQ101=sQuery(id+"F5.wireOp",EDGE,"E18.8.4");var subQ102=sQuery(id+"F5.wireOp",EDGE,"E10");var subQ103=sQuery(id+"F5.wireOp",EDGE,"E18.15.4");var subQ104=sQuery(id+"F5.wireOp",EDGE,"E18.1.4");var subQ105=sQuery(id+"F5.wireOp",EDGE,"E15.MirrorCS");var subQ106=sQuery(id+"F5.wireOp",EDGE,"E18.1.1");var subQ107=sQuery(id+"F5.wireOp",EDGE,"E18.9.4");var subQ108=sQuery(id+"F5.wireOp",EDGE,"E18.3.1");var subQ109=sQuery(id+"F5.wireOp",EDGE,"E18.2.2");var subQ110=sQuery(id+"F5.wireOp",EDGE,"E18.2.4");var subQ111=sQuery(id+"F5.wireOp",EDGE,"E18.13.3");var subQ112=sQuery(id+"F5.wireOp",EDGE,"E18.18.2");var subQ113=sQuery(id+"F5.wireOp",EDGE,"E18.11.3");var subQ114=sQuery(id+"F5.wireOp",EDGE,"E18.16.2");var subQ115=sQuery(id+"F5.wireOp",EDGE,"E18.11.4");var subQ116=sQuery(id+"F5.wireOp",EDGE,"E18.12.1");var subQ117=sQuery(id+"F5.wireOp",EDGE,"E18.20.3");var subQ118=sQuery(id+"F5.wireOp",EDGE,"E18.12.2");var subQ119=sQuery(id+"F5.wireOp",EDGE,"E18.12.3");var subQ120=sQuery(id+"F5.wireOp",EDGE,"E18.12.4");var subQ121=sQuery(id+"F5.wireOp",EDGE,"E18.23.3");var subQ122=sQuery(id+"F5.wireOp",EDGE,"E18.13.1");var subQ123=sQuery(id+"F5.wireOp",EDGE,"E18.14.1");var subQ124=sQuery(id+"F5.wireOp",EDGE,"E18.14.2");var subQ125=sQuery(id+"F5.wireOp",EDGE,"E18.14.3");var subQ126=sQuery(id+"F5.wireOp",EDGE,"E18.25.2");var subQ127=sQuery(id+"F5.wireOp",EDGE,"E18.14.4");var subQ128=sQuery(id+"F5.wireOp",EDGE,"E18.19.3");var subQ129=sQuery(id+"F5.wireOp",EDGE,"E18.18.3");var subQ130=sQuery(id+"F5.wireOp",EDGE,"E18.23.2");var subQ131=sQuery(id+"F5.wireOp",EDGE,"E18.15.1");var subQ132=sQuery(id+"F5.wireOp",EDGE,"E18.16.1");var subQ133=sQuery(id+"F5.wireOp",EDGE,"E18.16.3");var subQ134=sQuery(id+"F5.wireOp",EDGE,"E18.21.2");var subQ135=sQuery(id+"F5.wireOp",EDGE,"E18.16.4");var subQ136=sQuery(id+"F5.wireOp",EDGE,"E18.21.3");var subQ137=sQuery(id+"F5.wireOp",EDGE,"E18.17.1");var subQ138=sQuery(id+"F5.wireOp",EDGE,"E18.17.2");var subQ139=sQuery(id+"F5.wireOp",EDGE,"E18.17.3");var subQ140=sQuery(id+"F5.wireOp",EDGE,"E18.17.4");var subQ141=sQuery(id+"F5.wireOp",EDGE,"E18.21.1");var subQ142=sQuery(id+"F5.wireOp",EDGE,"E18.18.4");var subQ143=sQuery(id+"F5.wireOp",EDGE,"E18.19.1");var subQ144=sQuery(id+"F5.wireOp",EDGE,"E18.19.2");var subQ145=sQuery(id+"F5.wireOp",EDGE,"E18.19.4");var subQ146=sQuery(id+"F5.wireOp",EDGE,"E18.20.1");var subQ147=sQuery(id+"F5.wireOp",EDGE,"E18.20.4");var subQ148=sQuery(id+"F5.wireOp",EDGE,"E18.21.4");var subQ149=sQuery(id+"F5.wireOp",EDGE,"E18.24.2");var subQ150=sQuery(id+"F5.wireOp",EDGE,"E18.22.1");var subQ151=sQuery(id+"F5.wireOp",EDGE,"E21");var subQ152=sQuery(id+"F5.wireOp",EDGE,"E18.22.2");var subQ153=sQuery(id+"F5.wireOp",EDGE,"E18.22.3");var subQ154=sQuery(id+"F5.wireOp",EDGE,"E18.22.4");var subQ155=sQuery(id+"F5.wireOp",EDGE,"E18.23.1");var subQ156=sQuery(id+"F5.wireOp",EDGE,"E18.23.4");var subQ157=sQuery(id+"F5.wireOp",EDGE,"E18.24.1");var subQ158=sQuery(id+"F5.wireOp",EDGE,"E18.24.3");var subQ159=sQuery(id+"F5.wireOp",EDGE,"E18.24.4");var subQ160=sQuery(id+"F5.wireOp",EDGE,"E18.25.1");var subQ161=sQuery(id+"F5.wireOp",EDGE,"E18.26.1");var subQ162=sQuery(id+"F5.wireOp",EDGE,"E18.26.2");var subQ163=sQuery(id+"F5.wireOp",EDGE,"E18.26.3");var subQ164=sQuery(id+"F5.wireOp",EDGE,"E18.26.4");Q1=makeQuery(id+"F8.boolean.opBoolean","SPLIT",FACE,{"disambiguationData":[TD([makeQuery(id+"F6.opExtrude","SWEPT_FACE",FACE,{"disambiguationData":[OSD([subQ102])]})])],"derivedFrom":makeQuery(id+"F6.opExtrude","CAP_FACE",FACE,{"disambiguationData":[OSD([subQ28,subQ102,subQ83,subQ52,subQ105,subQ70,subQ88,subQ89,subQ106,subQ85,subQ47,subQ104,subQ75,subQ57,subQ16,subQ109,subQ67,subQ110,subQ91,subQ92,subQ108,subQ39,subQ37,subQ36,subQ35,subQ33,subQ32,subQ30,subQ24,subQ5,subQ23,subQ20,subQ59,subQ87,subQ19,subQ90,subQ44,subQ45,subQ43,subQ46,subQ71,subQ18,subQ17,subQ14,subQ79,subQ12,subQ10,subQ9,subQ31,subQ26,subQ40,subQ38,subQ21,subQ101,subQ34,subQ62,subQ8,subQ7,subQ4,subQ107,subQ2,subQ76,subQ0,subQ97,subQ15,subQ56,subQ55,subQ58,subQ65,subQ72,subQ113,subQ115,subQ53,subQ54,subQ116,subQ118,subQ119,subQ120,subQ48,subQ49,subQ122,subQ22,subQ111,subQ66,subQ41,subQ42,subQ123,subQ124,subQ125,subQ127,subQ50,subQ51,subQ131,subQ25,subQ100,subQ103,subQ11,subQ60,subQ132,subQ114,subQ133,subQ135,subQ93,subQ94,subQ137,subQ138,subQ139,subQ140,subQ95,subQ96,subQ68,subQ112,subQ129,subQ142,subQ27,subQ29,subQ143,subQ144,subQ128,subQ145,subQ98,subQ99,subQ146,subQ6,subQ117,subQ147,subQ61,subQ1,subQ141,subQ134,subQ136,subQ148,subQ73,subQ74,subQ150,subQ152,subQ153,subQ154,subQ69,subQ13,subQ155,subQ130,subQ121,subQ156,subQ63,subQ64,subQ157,subQ149,subQ158,subQ159,subQ77,subQ78,subQ160,subQ126,subQ3,subQ86,subQ80,subQ81,subQ161,subQ162,subQ163,subQ164,subQ84,subQ151])],"isStart":true})});}
            chamfer(context, id + "F7", {"entities" : qUnion([Q0, Q1]), "width" : .6 * mm, "tangentPropagation" : true});
        }
        {
            var Q0;
            Q0=makeQuery(id+"F5.imprint","IMPRINT",FACE,{"disambiguationData":[TD([[makeQuery(id+"F5.imprint","IMPRINT",EDGE,{"derivedFrom":sQuery(id+"F5.wireOp",EDGE,"E19")}),-1.0]])]});
            extrude(context, id + "F8", {"entities" : qUnion([Q0]), "operationType" : NewBodyOperationType.ADD, "oppositeDirection" : true, "depth" : (getVariable(context, 'CollarThickness')) * mm});
        }
        {
            var Q0;
            Q0=makeQuery(id+"F5.imprint","IMPRINT",FACE,{"disambiguationData":[TD([[makeQuery(id+"F5.imprint","IMPRINT",EDGE,{"derivedFrom":sQuery(id+"F5.wireOp",EDGE,"E19")}),1.0]])]});
            extrude(context, id + "F9", {"entities" : qUnion([Q0]), "operationType" : NewBodyOperationType.ADD, "oppositeDirection" : true, "depth" : (getVariable(context, 'ClampThickness') + getVariable(context, 'CollarThickness') + 5) * mm});
        }
        {
            var Q0;
            Q0=qCreatedBy(makeId("Front.planeOp"),FACE);
            var sketch = newSketch(context, id + "F10", { "sketchPlane" : qUnion([Q0])});
            skLineSegment(sketch, "E22.0", {"start": v(-4.85, -29.1) * mm, "end": v(4.85, -29.1) * mm, "construction": true});
            skLineSegment(sketch, "E22.1", {"start": v(-7.85, -4.1) * mm, "end": v(7.85, -4.1) * mm, "construction": true});
            skLineSegment(sketch, "E23", {"start": v(0, -4.1) * mm, "end": v(0, -29.1) * mm, "construction": true});
            skPoint(sketch, "E24", {"position": v(0, -24.1) * mm});
            skCircle(sketch, "E25", {"center": v(0, -25.43) * mm, "radius": 1.02 * mm});
            skSolve(sketch);
        }
        {
            var Q0;
            Q0=makeQuery(id+"F10.imprint","IMPRINT",FACE,{"disambiguationData":[TD([[makeQuery(id+"F10.imprint","IMPRINT",EDGE,{"derivedFrom":sQuery(id+"F10.wireOp",EDGE,"E25")}),1.0]])]});
            extrude(context, id + "F11", {"entities" : qUnion([Q0]), "operationType" : NewBodyOperationType.REMOVE, "endBound" : BoundingType.THROUGH_ALL, "oppositeDirection" : true, "depth" : 25 * mm, "hasSecondDirection" : true, "secondDirectionBound" : SecondDirectionBoundingType.THROUGH_ALL, "secondDirectionOppositeDirection" : false, "secondDirectionDepth" : 25 * mm});
        }
        {
            var Q0;
            Q0=makeQuery(id+"F8.opExtrude","CAP_EDGE",EDGE,{"disambiguationData":[OSD([sQuery(id+"F5.wireOp",EDGE,"E20.0")])],"isStart":false});
            chamfer(context, id + "F12", {"entities" : qUnion([Q0]), "width" : 1 * mm, "tangentPropagation" : true});
        }
    });
